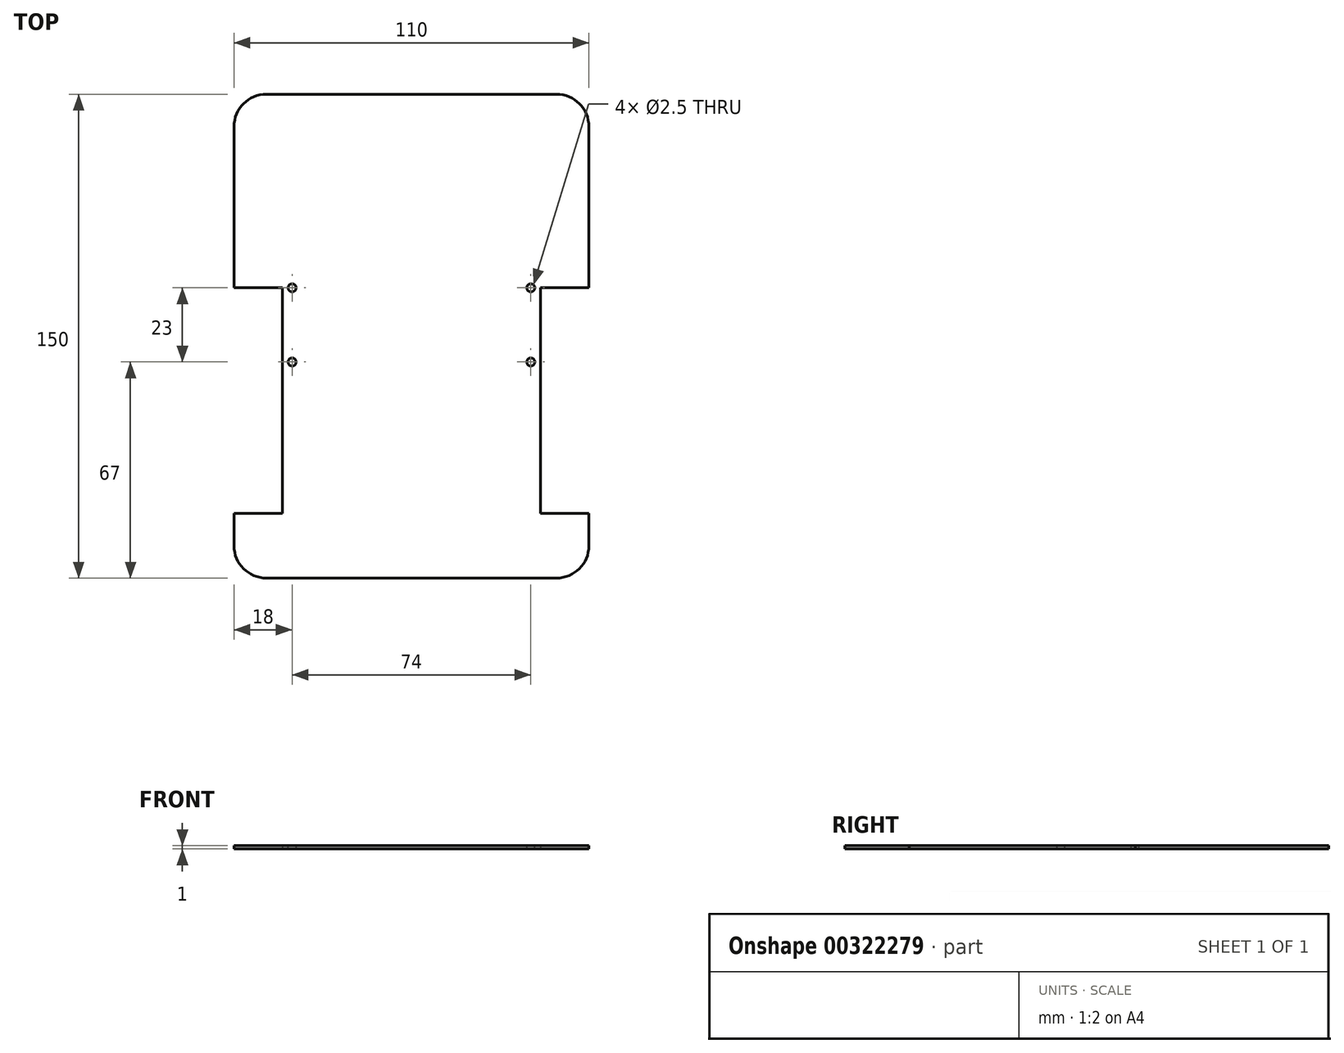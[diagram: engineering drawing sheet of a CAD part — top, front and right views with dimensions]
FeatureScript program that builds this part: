
annotation { "Feature Type Name" : "Feature", "Feature Type Description" : "" }
export const myFeature = defineFeature(function(context is Context, id is Id, definition is map)
    precondition{}
    {
        {
            var Q0;
            Q0=qCreatedBy(makeId("Top.planeOp"),FACE);
            var sketch = newSketch(context, id + "F0", { "sketchPlane" : qUnion([Q0])});
            skLineSegment(sketch, "E0", {"start": v(-45, 0) * mm, "end": v(45, 0) * mm});
            skLineSegment(sketch, "E1", {"start": v(-55, -10) * mm, "end": v(-55, -60) * mm});
            skLineSegment(sketch, "E2", {"start": v(55, -10) * mm, "end": v(55, -60) * mm});
            skLineSegment(sketch, "E3", {"start": v(-55, -60) * mm, "end": v(-40, -60) * mm});
            skLineSegment(sketch, "E4", {"start": v(-40, -60) * mm, "end": v(-40, -60) * mm});
            skLineSegment(sketch, "E5", {"start": v(-40, -60) * mm, "end": v(-40, -130) * mm});
            skLineSegment(sketch, "E6", {"start": v(-40, -130) * mm, "end": v(-55, -130) * mm});
            skLineSegment(sketch, "E7", {"start": v(-55, -130) * mm, "end": v(-55, -130) * mm});
            skLineSegment(sketch, "E8", {"start": v(-55, -130) * mm, "end": v(-55, -140) * mm});
            skLineSegment(sketch, "E9", {"start": v(-45, -150) * mm, "end": v(45, -150) * mm});
            skLineSegment(sketch, "E10", {"start": v(55, -140) * mm, "end": v(55, -130) * mm});
            skLineSegment(sketch, "E11", {"start": v(55, -130) * mm, "end": v(40, -130) * mm});
            skLineSegment(sketch, "E12", {"start": v(40, -130) * mm, "end": v(40, -60) * mm});
            skLineSegment(sketch, "E13", {"start": v(40, -60) * mm, "end": v(55, -60) * mm});
            skPoint(sketch, "E14.visualSharp", {"position": v(55, 0) * mm});
            skArc(sketch, "E14.filletArc", {"start": v(55, -10) * mm, "mid": v(52.07, -2.93) * mm, "end": v(45, 0) * mm});
            skPoint(sketch, "E15.visualSharp", {"position": v(-55, 0) * mm});
            skArc(sketch, "E15.filletArc", {"start": v(-45, 0) * mm, "mid": v(-52.07, -2.93) * mm, "end": v(-55, -10) * mm});
            skPoint(sketch, "E16.visualSharp", {"position": v(-55, -150) * mm});
            skArc(sketch, "E16.filletArc", {"start": v(-55, -140) * mm, "mid": v(-52.07, -147.07) * mm, "end": v(-45, -150) * mm});
            skPoint(sketch, "E17.visualSharp", {"position": v(55, -150) * mm});
            skArc(sketch, "E17.filletArc", {"start": v(45, -150) * mm, "mid": v(52.07, -147.07) * mm, "end": v(55, -140) * mm});
            skSolve(sketch);
        }
        {
            var Q0;
            Q0=makeQuery(id+"F0.imprint","IMPRINT",FACE,{"disambiguationData":[TD([[makeQuery(id+"F0.imprint","IMPRINT",EDGE,{"derivedFrom":sQuery(id+"F0.wireOp",EDGE,"E0")}),-1.0]])]});
            extrude(context, id + "F1", {"entities" : qUnion([Q0]), "depth" : 1 * mm});
        }
        {
            var Q0;
            Q0=makeQuery(id+"F1.opExtrude","CAP_FACE",FACE,{"disambiguationData":[OSD([sQuery(id+"F0.wireOp",EDGE,"E0"),sQuery(id+"F0.wireOp",EDGE,"E1"),sQuery(id+"F0.wireOp",EDGE,"E2"),sQuery(id+"F0.wireOp",EDGE,"E3"),sQuery(id+"F0.wireOp",EDGE,"E5"),sQuery(id+"F0.wireOp",EDGE,"E6"),sQuery(id+"F0.wireOp",EDGE,"E8"),sQuery(id+"F0.wireOp",EDGE,"E9"),sQuery(id+"F0.wireOp",EDGE,"E10"),sQuery(id+"F0.wireOp",EDGE,"E11"),sQuery(id+"F0.wireOp",EDGE,"E12"),sQuery(id+"F0.wireOp",EDGE,"E13"),sQuery(id+"F0.wireOp",EDGE,"E14.filletArc"),sQuery(id+"F0.wireOp",EDGE,"E15.filletArc"),sQuery(id+"F0.wireOp",EDGE,"E16.filletArc"),sQuery(id+"F0.wireOp",EDGE,"E17.filletArc")])],"isStart":false});
            var sketch = newSketch(context, id + "F2", { "sketchPlane" : qUnion([Q0])});
            skPoint(sketch, "E18.center.orphan", {"position": v(37, -60) * mm});
            skPoint(sketch, "E19.center.orphan", {"position": v(37, -83) * mm});
            skPoint(sketch, "E20.center.orphan", {"position": v(-37, -60) * mm});
            skPoint(sketch, "E21.center.orphan", {"position": v(-37, -83) * mm});
            skSolve(sketch);
        }
        {
            var Q0;
            Q0=sQuery(id+"F2.wireOp",VERTEX,"E18.center");
            var Q1;
            Q1=sQuery(id+"F2.wireOp",VERTEX,"E18.center.orphan");
            var Q2;
            Q2=sQuery(id+"F2.wireOp",VERTEX,"E19.center.orphan");
            var Q3;
            Q3=sQuery(id+"F2.wireOp",VERTEX,"E20.center.orphan");
            var Q4;
            Q4=sQuery(id+"F2.wireOp",VERTEX,"E21.center.orphan");
            var Q5;
            Q5=makeQuery(id+"F1.opExtrude","SWEPT_BODY",BODY,{"disambiguationData":[OSD([sQuery(id+"F0.wireOp",EDGE,"E0"),sQuery(id+"F0.wireOp",EDGE,"E1"),sQuery(id+"F0.wireOp",EDGE,"E2"),sQuery(id+"F0.wireOp",EDGE,"E3"),sQuery(id+"F0.wireOp",EDGE,"E5"),sQuery(id+"F0.wireOp",EDGE,"E6"),sQuery(id+"F0.wireOp",EDGE,"E8"),sQuery(id+"F0.wireOp",EDGE,"E9"),sQuery(id+"F0.wireOp",EDGE,"E10"),sQuery(id+"F0.wireOp",EDGE,"E11"),sQuery(id+"F0.wireOp",EDGE,"E12"),sQuery(id+"F0.wireOp",EDGE,"E13"),sQuery(id+"F0.wireOp",EDGE,"E14.filletArc"),sQuery(id+"F0.wireOp",EDGE,"E15.filletArc"),sQuery(id+"F0.wireOp",EDGE,"E16.filletArc"),sQuery(id+"F0.wireOp",EDGE,"E17.filletArc")])]});
            hole(context, id + "F3", {"style" : HoleStyle.SIMPLE, "endStyle" : HoleEndStyle.THROUGH, "standardTappedOrClearance" : lookupTablePath({ "fit" : "Normal", "standard" : "ISO", "size" : "2.5", "type" : "Drilled" }), "standardBlindInLast" : lookupTablePath({ "fit" : "Standard", "standard" : "ISO", "size" : "2.5", "type" : "Drilled" }), "holeDiameter" : 2.5 * mm, "tappedDepth" : 12 * mm, "tapClearance" : 3, "locations" : qUnion([Q0, Q1, Q2, Q3, Q4]), "scope" : qUnion([Q5])});
        }
    });
